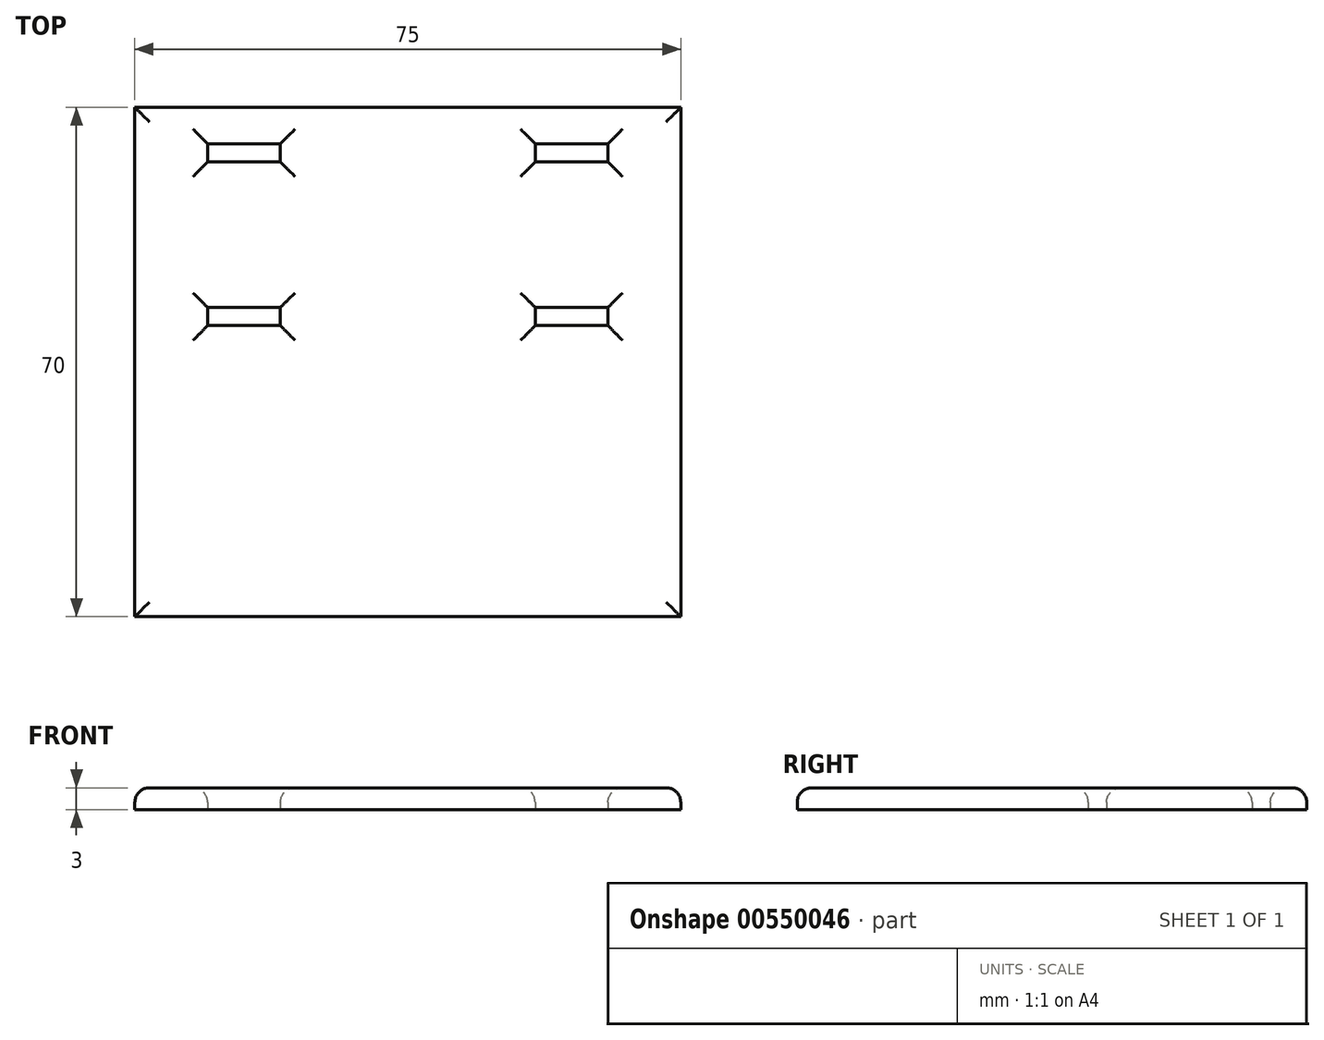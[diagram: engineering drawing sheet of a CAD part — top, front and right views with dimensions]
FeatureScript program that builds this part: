
annotation { "Feature Type Name" : "Feature", "Feature Type Description" : "" }
export const myFeature = defineFeature(function(context is Context, id is Id, definition is map)
    precondition{}
    {
        {
            var Q0;
            Q0=qCreatedBy(makeId("Top.planeOp"),FACE);
            var sketch = newSketch(context, id + "F0", { "sketchPlane" : qUnion([Q0])});
            skLineSegment(sketch, "E0", {"start": v(6.38, 5.31) * mm, "end": v(-8.62, 5.31) * mm, "construction": true});
            skLineSegment(sketch, "E1.bottom", {"start": v(-1.12, 5.31) * mm, "end": v(36.38, 5.31) * mm});
            skLineSegment(sketch, "E1.top", {"start": v(-1.12, -54.69) * mm, "end": v(36.38, -54.69) * mm});
            skLineSegment(sketch, "E1.left", {"start": v(-1.12, 5.31) * mm, "end": v(-1.12, -54.69) * mm, "construction": true});
            skLineSegment(sketch, "E1.right", {"start": v(36.38, 5.31) * mm, "end": v(36.38, -54.69) * mm});
            skLineSegment(sketch, "E2.bottom", {"start": v(-1.12, 5.31) * mm, "end": v(36.38, 5.31) * mm, "construction": true});
            skLineSegment(sketch, "E2.top", {"start": v(-1.12, 15.31) * mm, "end": v(36.38, 15.31) * mm});
            skLineSegment(sketch, "E2.left", {"start": v(-1.12, 5.31) * mm, "end": v(-1.12, 15.31) * mm});
            skLineSegment(sketch, "E2.right", {"start": v(36.38, 5.31) * mm, "end": v(36.38, 15.31) * mm});
            skLineSegment(sketch, "E3.bottom", {"start": v(-1.12, 5.31) * mm, "end": v(-38.62, 5.31) * mm, "construction": true});
            skLineSegment(sketch, "E3.top", {"start": v(-1.12, 15.31) * mm, "end": v(-38.62, 15.31) * mm});
            skLineSegment(sketch, "E3.left", {"start": v(-1.12, 5.31) * mm, "end": v(-1.12, 15.31) * mm, "construction": true});
            skLineSegment(sketch, "E3.right", {"start": v(-38.62, 5.31) * mm, "end": v(-38.62, 15.31) * mm});
            skLineSegment(sketch, "E4.bottom", {"start": v(-1.12, 5.31) * mm, "end": v(-38.62, 5.31) * mm});
            skLineSegment(sketch, "E4.top", {"start": v(-1.12, -54.69) * mm, "end": v(-38.62, -54.69) * mm});
            skLineSegment(sketch, "E4.left", {"start": v(-1.12, 5.31) * mm, "end": v(-1.12, -54.69) * mm});
            skLineSegment(sketch, "E4.right", {"start": v(-38.62, 5.31) * mm, "end": v(-38.62, -54.69) * mm});
            skLineSegment(sketch, "E5", {"start": v(-38.62, -54.69) * mm, "end": v(-38.62, 15.31) * mm, "construction": true});
            skLineSegment(sketch, "E6", {"start": v(36.38, 15.31) * mm, "end": v(-38.62, 15.31) * mm, "construction": true});
            skLineSegment(sketch, "E7.bottom", {"start": v(-28.62, 7.81) * mm, "end": v(-18.62, 7.81) * mm});
            skLineSegment(sketch, "E7.top", {"start": v(-28.62, 10.31) * mm, "end": v(-18.62, 10.31) * mm});
            skLineSegment(sketch, "E7.left", {"start": v(-28.62, 7.81) * mm, "end": v(-28.62, 10.31) * mm});
            skLineSegment(sketch, "E7.right", {"start": v(-18.62, 7.81) * mm, "end": v(-18.62, 10.31) * mm});
            skLineSegment(sketch, "E8.bottom", {"start": v(16.38, 7.81) * mm, "end": v(26.38, 7.81) * mm});
            skLineSegment(sketch, "E8.top", {"start": v(16.38, 10.31) * mm, "end": v(26.38, 10.31) * mm});
            skLineSegment(sketch, "E8.left", {"start": v(16.38, 7.81) * mm, "end": v(16.38, 10.31) * mm});
            skLineSegment(sketch, "E8.right", {"start": v(26.38, 7.81) * mm, "end": v(26.38, 10.31) * mm});
            skLineSegment(sketch, "E9.bottom", {"start": v(16.38, -14.69) * mm, "end": v(26.38, -14.69) * mm});
            skLineSegment(sketch, "E9.top", {"start": v(16.38, -12.19) * mm, "end": v(26.38, -12.19) * mm});
            skLineSegment(sketch, "E9.left", {"start": v(16.38, -14.69) * mm, "end": v(16.38, -12.19) * mm});
            skLineSegment(sketch, "E9.right", {"start": v(26.38, -14.69) * mm, "end": v(26.38, -12.19) * mm});
            skLineSegment(sketch, "E10.bottom", {"start": v(-28.62, -14.69) * mm, "end": v(-18.62, -14.69) * mm});
            skLineSegment(sketch, "E10.top", {"start": v(-28.62, -12.19) * mm, "end": v(-18.62, -12.19) * mm});
            skLineSegment(sketch, "E10.left", {"start": v(-28.62, -14.69) * mm, "end": v(-28.62, -12.19) * mm});
            skLineSegment(sketch, "E10.right", {"start": v(-18.62, -14.69) * mm, "end": v(-18.62, -12.19) * mm});
            skLineSegment(sketch, "E11", {"start": v(16.38, -14.69) * mm, "end": v(16.38, -54.69) * mm, "construction": true});
            skLineSegment(sketch, "E12", {"start": v(-18.62, -14.69) * mm, "end": v(-18.62, -54.69) * mm, "construction": true});
            skLineSegment(sketch, "E13", {"start": v(16.38, 10.31) * mm, "end": v(16.38, 15.31) * mm, "construction": true});
            skLineSegment(sketch, "E14", {"start": v(-18.62, 10.31) * mm, "end": v(-18.62, 15.31) * mm, "construction": true});
            skLineSegment(sketch, "E15", {"start": v(26.38, -14.69) * mm, "end": v(36.38, -14.69) * mm, "construction": true});
            skLineSegment(sketch, "E16", {"start": v(26.38, 10.31) * mm, "end": v(36.38, 10.31) * mm, "construction": true});
            skLineSegment(sketch, "E17", {"start": v(-28.62, 10.31) * mm, "end": v(-38.62, 10.31) * mm, "construction": true});
            skLineSegment(sketch, "E18", {"start": v(-28.62, -12.19) * mm, "end": v(-38.62, -12.19) * mm, "construction": true});
            skSolve(sketch);
        }
        {
            var Q0;
            Q0 = qSketchRegion(id + "F0", true);
            extrude(context, id + "F1", {"entities" : qUnion([Q0]), "depth" : 3 * mm, "offsetDistance" : 25 * mm});
        }
        {
            var Q0;
            Q0=makeQuery(id+"F1.opExtrude","CAP_EDGE",EDGE,{"disambiguationData":[OSD([sQuery(id+"F0.wireOp",EDGE,"E2.top"),sQuery(id+"F0.wireOp",EDGE,"E3.top")])],"isStart":false});
            var Q1;
            Q1=makeQuery(id+"F1.opExtrude","CAP_EDGE",EDGE,{"disambiguationData":[OSD([sQuery(id+"F0.wireOp",EDGE,"E3.right"),sQuery(id+"F0.wireOp",EDGE,"E4.right")])],"isStart":false});
            var Q2;
            Q2=makeQuery(id+"F1.opExtrude","CAP_EDGE",EDGE,{"disambiguationData":[OSD([sQuery(id+"F0.wireOp",EDGE,"E7.top")])],"isStart":false});
            var Q3;
            Q3=makeQuery(id+"F1.opExtrude","CAP_EDGE",EDGE,{"disambiguationData":[OSD([sQuery(id+"F0.wireOp",EDGE,"E7.bottom")])],"isStart":false});
            var Q4;
            Q4=makeQuery(id+"F1.opExtrude","CAP_EDGE",EDGE,{"disambiguationData":[OSD([sQuery(id+"F0.wireOp",EDGE,"E7.right")])],"isStart":false});
            var Q5;
            Q5=makeQuery(id+"F1.opExtrude","CAP_EDGE",EDGE,{"disambiguationData":[OSD([sQuery(id+"F0.wireOp",EDGE,"E7.left")])],"isStart":false});
            var Q6;
            Q6=makeQuery(id+"F1.opExtrude","CAP_FACE",FACE,{"disambiguationData":[OSD([sQuery(id+"F0.wireOp",EDGE,"E1.top"),sQuery(id+"F0.wireOp",EDGE,"E1.right"),sQuery(id+"F0.wireOp",EDGE,"E2.top"),sQuery(id+"F0.wireOp",EDGE,"E2.right"),sQuery(id+"F0.wireOp",EDGE,"E3.top"),sQuery(id+"F0.wireOp",EDGE,"E3.right"),sQuery(id+"F0.wireOp",EDGE,"E4.top"),sQuery(id+"F0.wireOp",EDGE,"E4.right"),sQuery(id+"F0.wireOp",EDGE,"E7.bottom"),sQuery(id+"F0.wireOp",EDGE,"E7.top"),sQuery(id+"F0.wireOp",EDGE,"E7.left"),sQuery(id+"F0.wireOp",EDGE,"E7.right"),sQuery(id+"F0.wireOp",EDGE,"E8.bottom"),sQuery(id+"F0.wireOp",EDGE,"E8.top"),sQuery(id+"F0.wireOp",EDGE,"E8.left"),sQuery(id+"F0.wireOp",EDGE,"E8.right"),sQuery(id+"F0.wireOp",EDGE,"E9.bottom"),sQuery(id+"F0.wireOp",EDGE,"E9.top"),sQuery(id+"F0.wireOp",EDGE,"E9.left"),sQuery(id+"F0.wireOp",EDGE,"E9.right"),sQuery(id+"F0.wireOp",EDGE,"E10.bottom"),sQuery(id+"F0.wireOp",EDGE,"E10.top"),sQuery(id+"F0.wireOp",EDGE,"E10.left"),sQuery(id+"F0.wireOp",EDGE,"E10.right")])],"isStart":false});
            fillet(context, id + "F2", {"entities" : qUnion([Q0, Q1, Q2, Q3, Q4, Q5, Q6]), "radius" : 2 * mm, "tangentPropagation" : true, "allowEdgeOverflow" : false});
        }
    });
